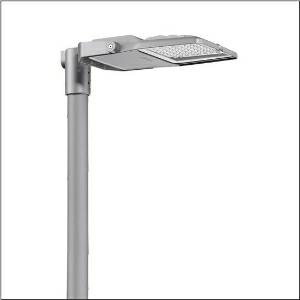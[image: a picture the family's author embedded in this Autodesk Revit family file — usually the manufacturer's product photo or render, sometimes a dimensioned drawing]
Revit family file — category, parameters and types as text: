
# Revit family: floodlight_fl_21_mini___pl43_5xa7772b2a3a_847d
name_source: partatom
category: Lighting Fixtures
units: mm (PartAtom-declared; Revit-internal decimal feet)

## family parameters
Cut with Voids When Loaded = No
Host = Face
Light Source = No
Part Type = Normal
Room Calculation Point = No
Round Connector Dimension = Use Diameter
Shared = No

## types (1)
- --- (1 x LED, 6400 lm, 45.5 W, 3000K)
    Apparent Load = 46 VA
    CIE Flux Codes = 27 78 99 100 100
    Color Rendering = 70
    Color Temperature = 3000K
    Default Elevation = 1800 mm
    Description = Floodlight FL 21 mini, floodlight, primary light control with lens, of PMMA, primary optical cover: protective disc, of toughened safety glass, transparent, light distribution: PL43, light emission: direct distribution, installation type: surface-mounted, LED, High Power LED, rated luminous flux: 6.400lm, luminous efficacy: 141lm/W, light colour: 730, colour temperature: 3000K, control gear: ECG iQ, control: Auto-Match, Temp-Guard, Night-Set, Smart-Wire, Desk-Remote (wireless, voltage-free reading and setting of iQ features in the workshop via application-optimized NFC function/RFID function), optimised constant luminous flux control (CLO 2.0), Light-Fading, Lumen-Switch, with terminal, 6-pole, mains connection: 220..240V, AC, 50/60Hz, start of lifetime: 46W, end of lifetime: 48W, reduction: 22W, luminaire housing, of diecast aluminium, powder-coated, Siteco® metallic grey (DB 702S), corrosivity category C5 according to DIN EN ISO 12944, mast bracket, of steel, galvanised, powder-coated, protection rating (complete): IP66, insulation class (complete): insulation class II (safety insulation), certification: CE, ENEC, VDE, protection symbol: D, impact resistance: IK08, permissible operating ambient temperature: -40..+40°C, permissible operating ambient temperature for outdoor applications: -40..+50°C, standard: DIN EN 12944, packaging unit: 1 piece

Light Distribution: PL43
    Height = 70 mm
    Lamp = 1 x LED
    Lamp Light Flux = 6400 lm
    Lamp Power = 45.5 W
    Lamp count = 1
    Length = 485 mm
    Luminous efficacy = 141 lm/W
    Manufacturer = Siteco
    ModVariant = No
    Model = 5XA7772B2A3A
    Number of Poles = 1
    OnlyDefault = Yes
    Power Factor = 1
    Product Name = Floodlight FL 21 mini | PL43
    Product group = floodlight | pylon top
    ProductGroupID = 6101
    Protection Class = Protection class II
    Protection Degree = IP 66
    RLX_Detail_Level = 1
    RlxData = <blob elided: 100833 chars, md5=eec721f7>
    Socket = socket
    Standby Power = 0 W
    System Light Flux = 6400 lm
    System Power = 46 W
    Type Comments = factory setting: luminous flux: 100 % | dim-lin: 254 | 463 mA
    Type Image = l_1007125.jpg
    URL = http://relux.com
    VarID = @adj_073977
    Voltage = 0 V
    Weight = 0.00 kg
    Width = 337 mm

## geometry (parser evidence)
native form markers: Blend x4, Sweep x12
no freeform markers — native parametric forms only
